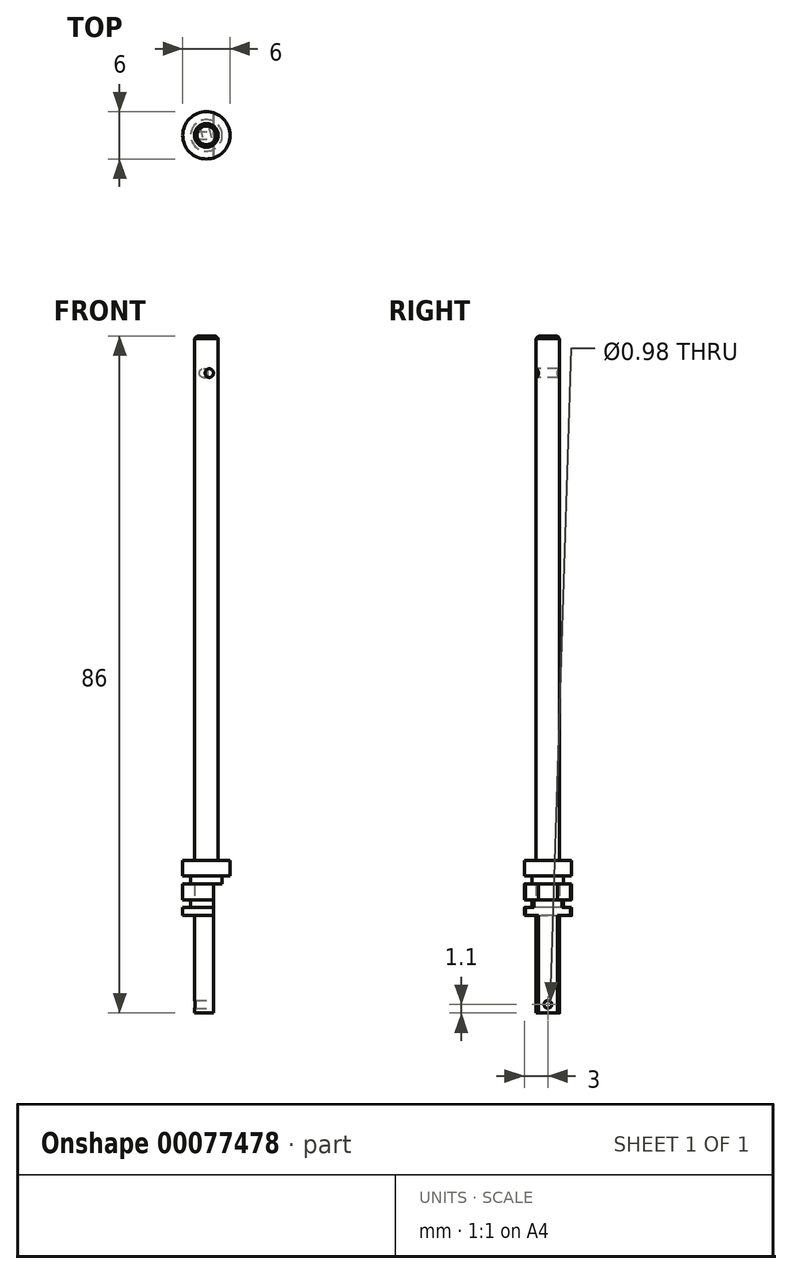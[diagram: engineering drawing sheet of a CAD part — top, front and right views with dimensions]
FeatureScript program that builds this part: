
annotation { "Feature Type Name" : "Feature", "Feature Type Description" : "" }
export const myFeature = defineFeature(function(context is Context, id is Id, definition is map)
    precondition{}
    {
        {
            var Q0;
            Q0=qCreatedBy(makeId("Top.planeOp"),FACE);
            var sketch = newSketch(context, id + "F0", { "sketchPlane" : qUnion([Q0])});
            skCircle(sketch, "E0", {"center": v(0, 0) * mm, "radius": 1.5 * mm});
            skSolve(sketch);
        }
        {
            var Q0;
            Q0=makeQuery(id+"F0.imprint","IMPRINT",FACE,{"disambiguationData":[TD([[makeQuery(id+"F0.imprint","IMPRINT",EDGE,{"derivedFrom":sQuery(id+"F0.wireOp",EDGE,"E0")}),1.0]])]});
            extrude(context, id + "F1", {"entities" : qUnion([Q0]), "depth" : 86 * mm});
        }
        {
            var Q0;
            Q0=makeQuery(id+"F1.opExtrude","CAP_EDGE",EDGE,{"disambiguationData":[OSD([sQuery(id+"F0.wireOp",EDGE,"E0")])],"isStart":false});
            chamfer(context, id + "F2", {"entities" : qUnion([Q0]), "width" : 0.3 * mm, "tangentPropagation" : true});
        }
        {
            var Q0;
            Q0=qCreatedBy(makeId("Front.planeOp"),FACE);
            var sketch = newSketch(context, id + "F3", { "sketchPlane" : qUnion([Q0])});
            skLineSegment(sketch, "E1", {"start": v(0, 0) * mm, "end": v(0, 86) * mm, "construction": true});
            skLineSegment(sketch, "E2", {"start": v(-3, 19.4) * mm, "end": v(0, 19.4) * mm});
            skLineSegment(sketch, "E3", {"start": v(-3, 19.4) * mm, "end": v(-3, 17.4) * mm});
            skLineSegment(sketch, "E4", {"start": v(-3, 17.4) * mm, "end": v(-2, 17.4) * mm});
            skLineSegment(sketch, "E5", {"start": v(-2, 13.4) * mm, "end": v(-3, 13.4) * mm});
            skLineSegment(sketch, "E6", {"start": v(-3, 13.4) * mm, "end": v(-3, 12.4) * mm});
            skLineSegment(sketch, "E7", {"start": v(-3, 12.4) * mm, "end": v(0, 12.4) * mm});
            skLineSegment(sketch, "E8", {"start": v(0, 19.4) * mm, "end": v(0, 12.4) * mm});
            skLineSegment(sketch, "E9", {"start": v(-2, 17.4) * mm, "end": v(-2, 16.4) * mm});
            skLineSegment(sketch, "E10", {"start": v(-2, 16.4) * mm, "end": v(0, 16.4) * mm});
            skLineSegment(sketch, "E11", {"start": v(0, 16.4) * mm, "end": v(0, 14.4) * mm});
            skLineSegment(sketch, "E12", {"start": v(0, 14.4) * mm, "end": v(-2, 14.4) * mm});
            skLineSegment(sketch, "E13", {"start": v(-2, 14.4) * mm, "end": v(-2, 13.4) * mm});
            skSolve(sketch);
        }
        {
            var Q0;
            {var subQ2=sQuery(id+"F3.wireOp",EDGE,"E2");Q0=makeQuery(id+"F3.imprint","IMPRINT",FACE,{"disambiguationData":[TD([[makeQuery(id+"F3.imprint","IMPRINT",EDGE,{"derivedFrom":subQ2}),-1.0]])]});}
            var Q1;
            Q1=makeQuery(id+"F3.imprint","IMPRINT",FACE,{"disambiguationData":[TD([[makeQuery(id+"F3.imprint","IMPRINT",EDGE,{"derivedFrom":sQuery(id+"F3.wireOp",EDGE,"E5")}),1.0]])]});
            var Q2;
            Q2=sQuery(id+"F3.wireOp",EDGE,"E8");
            revolve(context, id + "F4", {"operationType" : NewBodyOperationType.ADD, "entities" : qUnion([Q0, Q1]), "axis" : qUnion([Q2]), "revolveType" : RevolveType.FULL});
        }
        {
            var Q0;
            Q0=qCreatedBy(makeId("Front.planeOp"),FACE);
            var sketch = newSketch(context, id + "F5", { "sketchPlane" : qUnion([Q0])});
            skLineSegment(sketch, "E14", {"start": v(0, 16.4) * mm, "end": v(-3, 16.4) * mm});
            skLineSegment(sketch, "E15", {"start": v(-3, 16.4) * mm, "end": v(-3, 14.4) * mm});
            skLineSegment(sketch, "E16", {"start": v(-3, 14.4) * mm, "end": v(0, 14.4) * mm});
            skLineSegment(sketch, "E17", {"start": v(0, 14.4) * mm, "end": v(0, 16.4) * mm});
            skSolve(sketch);
        }
        {
            var Q0;
            Q0=makeQuery(id+"F5.imprint","IMPRINT",FACE,{"disambiguationData":[TD([[makeQuery(id+"F5.imprint","IMPRINT",EDGE,{"derivedFrom":sQuery(id+"F5.wireOp",EDGE,"E14")}),1.0]])]});
            var Q1;
            Q1=sQuery(id+"F3.wireOp",EDGE,"E8");
            revolve(context, id + "F6", {"entities" : qUnion([Q0]), "axis" : qUnion([Q1]), "revolveType" : RevolveType.SYMMETRIC, "angle" : 360 * degree});
        }
        {
            var Q0;
            Q0=makeQuery(id+"F6.opRevolve","SWEPT_FACE",FACE,{"disambiguationData":[OSD([sQuery(id+"F5.wireOp",EDGE,"E14")])]});
            var sketch = newSketch(context, id + "F7", { "sketchPlane" : qUnion([Q0])});
            skLineSegment(sketch, "E18", {"start": v(0.9, 2.86) * mm, "end": v(0.9, -2.86) * mm});
            skSolve(sketch);
        }
        {
            var Q0;
            {var subQ1=sQuery(id+"F7.wireOp",EDGE,"E18");Q0=makeQuery(id+"F7.imprint","IMPRINT",FACE,{"disambiguationData":[TD([[makeQuery(id+"F7.imprint","IMPRINT",EDGE,{"derivedFrom":subQ1}),1.0]])]});}
            extrude(context, id + "F8", {"entities" : qUnion([Q0]), "operationType" : NewBodyOperationType.REMOVE, "endBound" : BoundingType.THROUGH_ALL, "oppositeDirection" : true, "depth" : 25 * mm});
        }
        {
            var Q0;
            Q0=makeQuery(id+"F1.opExtrude","CAP_FACE",FACE,{"disambiguationData":[OSD([sQuery(id+"F0.wireOp",EDGE,"E0")])],"isStart":false});
            cPlane(context, id + "F9", {"entities" : qUnion([Q0]), "cplaneType" : CPlaneType.OFFSET, "offset" : 4.7 * mm, "oppositeDirection" : true, "width" : 150 * mm, "height" : 150 * mm});
        }
        {
            var Q0;
            Q0=qCreatedBy(id+"F9.planeOp",FACE);
            var sketch = newSketch(context, id + "F10", { "sketchPlane" : qUnion([Q0])});
            skLineSegment(sketch, "E19", {"start": v(-0.23, 3) * mm, "end": v(1.3, -2.7) * mm});
            skLineSegment(sketch, "E20", {"start": v(-0.78, 2.9) * mm, "end": v(0.78, -2.9) * mm});
            skArc(sketch, "E21", {"start": v(0.78, -2.9) * mm, "mid": v(1.04, -2.81) * mm, "end": v(1.3, -2.7) * mm});
            skArc(sketch, "E22.trimOffspring", {"start": v(-0.23, 3) * mm, "mid": v(-0.5, 2.96) * mm, "end": v(-0.78, 2.9) * mm});
            skSolve(sketch);
        }
        {
            var Q0;
            Q0=makeQuery(id+"F10.imprint","IMPRINT",FACE,{"disambiguationData":[TD([[makeQuery(id+"F10.imprint","IMPRINT",EDGE,{"derivedFrom":sQuery(id+"F10.wireOp",EDGE,"E19")}),-1.0]])]});
            var Q1;
            Q1=sQuery(id+"F10.wireOp",EDGE,"E20");
            revolve(context, id + "F11", {"operationType" : NewBodyOperationType.REMOVE, "entities" : qUnion([Q0]), "axis" : qUnion([Q1]), "revolveType" : RevolveType.FULL, "oppositeDirection" : true});
        }
        {
            var Q0;
            Q0=qCreatedBy(makeId("Top.planeOp"),FACE);
            cPlane(context, id + "F12", {"entities" : qUnion([Q0]), "cplaneType" : CPlaneType.OFFSET, "offset" : 1.1 * mm, "width" : 150 * mm, "height" : 150 * mm});
        }
        {
            var Q0;
            Q0=qCreatedBy(id+"F12.planeOp",FACE);
            var sketch = newSketch(context, id + "F13", { "sketchPlane" : qUnion([Q0])});
            skLineSegment(sketch, "E23", {"start": v(-3, 0) * mm, "end": v(3, 0) * mm});
            skLineSegment(sketch, "E24", {"start": v(2.96, 0.5) * mm, "end": v(-2.96, 0.49) * mm});
            skArc(sketch, "E25", {"start": v(-2.96, 0.49) * mm, "mid": v(-2.99, 0.25) * mm, "end": v(-3, 0) * mm});
            skArc(sketch, "E26.trimOffspring", {"start": v(3, 0) * mm, "mid": v(2.99, 0.25) * mm, "end": v(2.96, 0.5) * mm});
            skSolve(sketch);
        }
        {
            var Q0;
            Q0=makeQuery(id+"F13.imprint","IMPRINT",FACE,{"disambiguationData":[TD([[makeQuery(id+"F13.imprint","IMPRINT",EDGE,{"derivedFrom":sQuery(id+"F13.wireOp",EDGE,"E23")}),1.0]])]});
            var Q1;
            Q1=sQuery(id+"F13.wireOp",EDGE,"E23");
            revolve(context, id + "F14", {"operationType" : NewBodyOperationType.REMOVE, "entities" : qUnion([Q0]), "axis" : qUnion([Q1]), "revolveType" : RevolveType.FULL, "oppositeDirection" : true});
        }
    });
